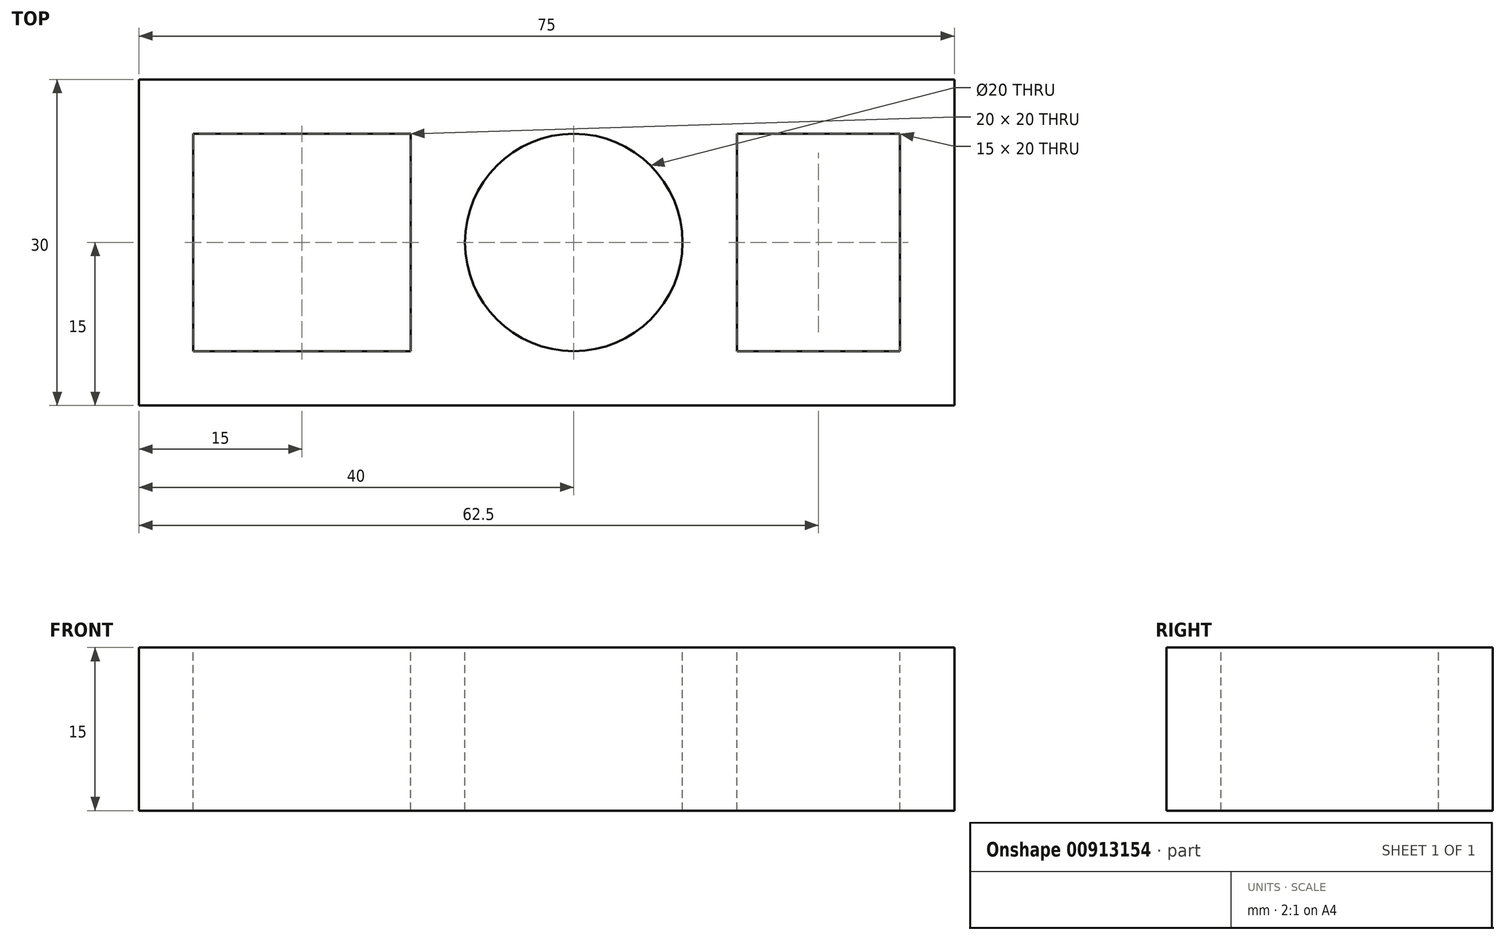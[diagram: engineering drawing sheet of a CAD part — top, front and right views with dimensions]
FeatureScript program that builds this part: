
annotation { "Feature Type Name" : "Feature", "Feature Type Description" : "" }
export const myFeature = defineFeature(function(context is Context, id is Id, definition is map)
    precondition{}
    {
        {
            var Q0;
            Q0=qCreatedBy(makeId("Front.planeOp"),FACE);
            var sketch = newSketch(context, id + "F0", { "sketchPlane" : qUnion([Q0])});
            skLineSegment(sketch, "E0.bottom", {"start": v(-15.9, 12.81) * mm, "end": v(59.1, 12.81) * mm});
            skLineSegment(sketch, "E0.top", {"start": v(-15.9, -2.19) * mm, "end": v(59.1, -2.19) * mm});
            skLineSegment(sketch, "E0.left", {"start": v(-15.9, 12.81) * mm, "end": v(-15.9, -2.19) * mm});
            skLineSegment(sketch, "E0.right", {"start": v(59.1, 12.81) * mm, "end": v(59.1, -2.19) * mm});
            skSolve(sketch);
        }
        {
            var Q0;
            Q0=makeQuery(id+"F0.imprint","IMPRINT",FACE,{"disambiguationData":[TD([[makeQuery(id+"F0.imprint","IMPRINT",EDGE,{"derivedFrom":sQuery(id+"F0.wireOp",EDGE,"E0.bottom")}),-1.0]])]});
            extrude(context, id + "F1", {"entities" : qUnion([Q0]), "depth" : 30 * mm, "offsetDistance" : 25.4 * mm});
        }
        {
            var Q0;
            Q0=makeQuery(id+"F1.opExtrude","SWEPT_FACE",FACE,{"disambiguationData":[OSD([sQuery(id+"F0.wireOp",EDGE,"E0.bottom")])]});
            var sketch = newSketch(context, id + "F2", { "sketchPlane" : qUnion([Q0])});
            skLineSegment(sketch, "E1.bottom", {"start": v(-10.9, -5) * mm, "end": v(9.1, -5) * mm});
            skLineSegment(sketch, "E1.top", {"start": v(-10.9, -25) * mm, "end": v(9.1, -25) * mm});
            skLineSegment(sketch, "E1.left", {"start": v(-10.9, -5) * mm, "end": v(-10.9, -25) * mm});
            skLineSegment(sketch, "E1.right", {"start": v(9.1, -5) * mm, "end": v(9.1, -25) * mm});
            skSolve(sketch);
        }
        {
            var Q0;
            Q0=makeQuery(id+"F2.imprint","IMPRINT",FACE,{"disambiguationData":[TD([[makeQuery(id+"F2.imprint","IMPRINT",EDGE,{"derivedFrom":sQuery(id+"F2.wireOp",EDGE,"E1.bottom")}),-1.0]])]});
            extrude(context, id + "F3", {"entities" : qUnion([Q0]), "operationType" : NewBodyOperationType.REMOVE, "oppositeDirection" : true, "depth" : 15 * mm, "offsetDistance" : 25.4 * mm});
        }
        {
            var Q0;
            Q0=makeQuery(id+"F1.opExtrude","SWEPT_FACE",FACE,{"disambiguationData":[OSD([sQuery(id+"F0.wireOp",EDGE,"E0.bottom")])]});
            var sketch = newSketch(context, id + "F4", { "sketchPlane" : qUnion([Q0])});
            skCircle(sketch, "E2", {"center": v(24.1, -15) * mm, "radius": 10 * mm});
            skSolve(sketch);
        }
        {
            var Q0;
            Q0=makeQuery(id+"F4.imprint","IMPRINT",FACE,{"disambiguationData":[TD([[makeQuery(id+"F4.imprint","IMPRINT",EDGE,{"derivedFrom":sQuery(id+"F4.wireOp",EDGE,"E2")}),1.0]])]});
            extrude(context, id + "F5", {"entities" : qUnion([Q0]), "operationType" : NewBodyOperationType.REMOVE, "oppositeDirection" : true, "depth" : 15 * mm, "offsetDistance" : 25.4 * mm});
        }
        {
            var Q0;
            Q0=makeQuery(id+"F1.opExtrude","SWEPT_FACE",FACE,{"disambiguationData":[OSD([sQuery(id+"F0.wireOp",EDGE,"E0.bottom")])]});
            var sketch = newSketch(context, id + "F6", { "sketchPlane" : qUnion([Q0])});
            skLineSegment(sketch, "E3.bottom", {"start": v(54.1, -25) * mm, "end": v(39.1, -25) * mm});
            skLineSegment(sketch, "E3.top", {"start": v(54.1, -5) * mm, "end": v(39.1, -5) * mm});
            skLineSegment(sketch, "E3.left", {"start": v(54.1, -25) * mm, "end": v(54.1, -5) * mm});
            skLineSegment(sketch, "E3.right", {"start": v(39.1, -25) * mm, "end": v(39.1, -5) * mm});
            skSolve(sketch);
        }
        {
            var Q0;
            Q0=makeQuery(id+"F6.imprint","IMPRINT",FACE,{"disambiguationData":[TD([[makeQuery(id+"F6.imprint","IMPRINT",EDGE,{"derivedFrom":sQuery(id+"F6.wireOp",EDGE,"E3.bottom")}),-1.0]])]});
            extrude(context, id + "F7", {"entities" : qUnion([Q0]), "operationType" : NewBodyOperationType.REMOVE, "oppositeDirection" : true, "depth" : 15 * mm, "offsetDistance" : 25.4 * mm});
        }
    });
